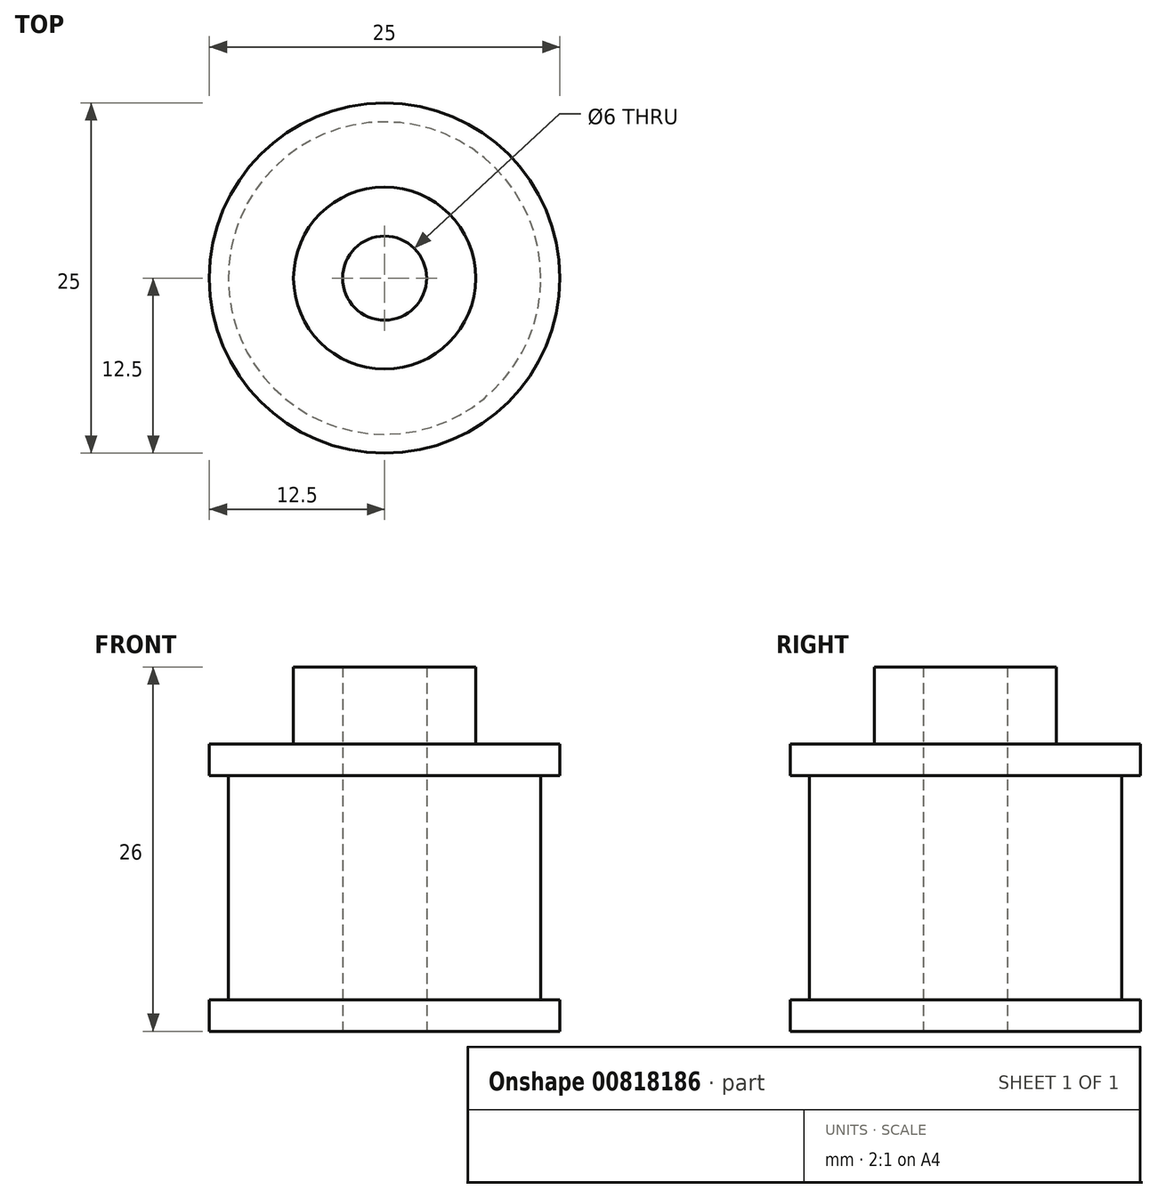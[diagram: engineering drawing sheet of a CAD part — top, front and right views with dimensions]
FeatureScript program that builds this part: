
annotation { "Feature Type Name" : "Feature", "Feature Type Description" : "" }
export const myFeature = defineFeature(function(context is Context, id is Id, definition is map)
    precondition{}
    {
        {
            var Q0;
            Q0=qCreatedBy(makeId("Top.planeOp"),FACE);
            var sketch = newSketch(context, id + "F0", { "sketchPlane" : qUnion([Q0])});
            skCircle(sketch, "E0", {"center": v(0, 0) * mm, "radius": 11.15 * mm});
            skCircle(sketch, "E1", {"center": v(0, 0) * mm, "radius": 12.5 * mm});
            skCircle(sketch, "E2", {"center": v(0, 0) * mm, "radius": 3 * mm});
            skCircle(sketch, "E3", {"center": v(0, 0) * mm, "radius": 6.5 * mm});
            skSolve(sketch);
        }
        {
            var Q0;
            Q0=makeQuery(id+"F0.imprint","IMPRINT",FACE,{"disambiguationData":[TD([[makeQuery(id+"F0.imprint","IMPRINT",EDGE,{"derivedFrom":sQuery(id+"F0.wireOp",EDGE,"E0")}),-1.0]])]});
            var Q1;
            Q1=makeQuery(id+"F0.imprint","IMPRINT",FACE,{"disambiguationData":[TD([[makeQuery(id+"F0.imprint","IMPRINT",EDGE,{"derivedFrom":sQuery(id+"F0.wireOp",EDGE,"E0")}),1.0]])]});
            var Q2;
            Q2=makeQuery(id+"F0.imprint","IMPRINT",FACE,{"disambiguationData":[TD([[makeQuery(id+"F0.imprint","IMPRINT",EDGE,{"derivedFrom":sQuery(id+"F0.wireOp",EDGE,"E2")}),-1.0]])]});
            extrude(context, id + "F1", {"entities" : qUnion([Q0, Q1, Q2]), "depth" : 20.5 * mm, "offsetDistance" : 25 * mm, "symmetric" : true});
        }
        {
            var Q0;
            Q0=makeQuery(id+"F0.imprint","IMPRINT",FACE,{"disambiguationData":[TD([[makeQuery(id+"F0.imprint","IMPRINT",EDGE,{"derivedFrom":sQuery(id+"F0.wireOp",EDGE,"E0")}),-1.0]])]});
            extrude(context, id + "F2", {"entities" : qUnion([Q0]), "operationType" : NewBodyOperationType.REMOVE, "oppositeDirection" : true, "depth" : 16 * mm, "offsetDistance" : 25 * mm, "symmetric" : true});
        }
        {
            var Q0;
            Q0=makeQuery(id+"F0.imprint","IMPRINT",FACE,{"disambiguationData":[TD([[makeQuery(id+"F0.imprint","IMPRINT",EDGE,{"derivedFrom":sQuery(id+"F0.wireOp",EDGE,"E2")}),-1.0]])]});
            extrude(context, id + "F3", {"entities" : qUnion([Q0]), "operationType" : NewBodyOperationType.ADD, "depth" : 15.75 * mm, "offsetDistance" : 25 * mm});
        }
    });
